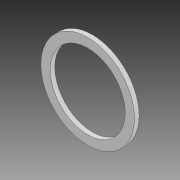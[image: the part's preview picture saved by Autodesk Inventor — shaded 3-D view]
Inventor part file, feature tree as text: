
AUTODESK INVENTOR PART (.ipt)
format: ipt  version: 2022 (Build 260153000, 153)  size: 83,968 bytes
history: native  units: mm
features: extrude x1, sketch x1
ambient origin geometry x8: Origin, YZ Plane, XZ Plane, XY Plane, X Axis, Y Axis, Z Axis, Center Point
bodies: Solid1 (feature_tree)
feature tree (2):
  extrude  "Extrusion1"  Depth=0.5mm
  sketch  "Sketch1"  dims[d0=8.1mm d1=1.0mm d2=0.5mm d3=0.0mm]
